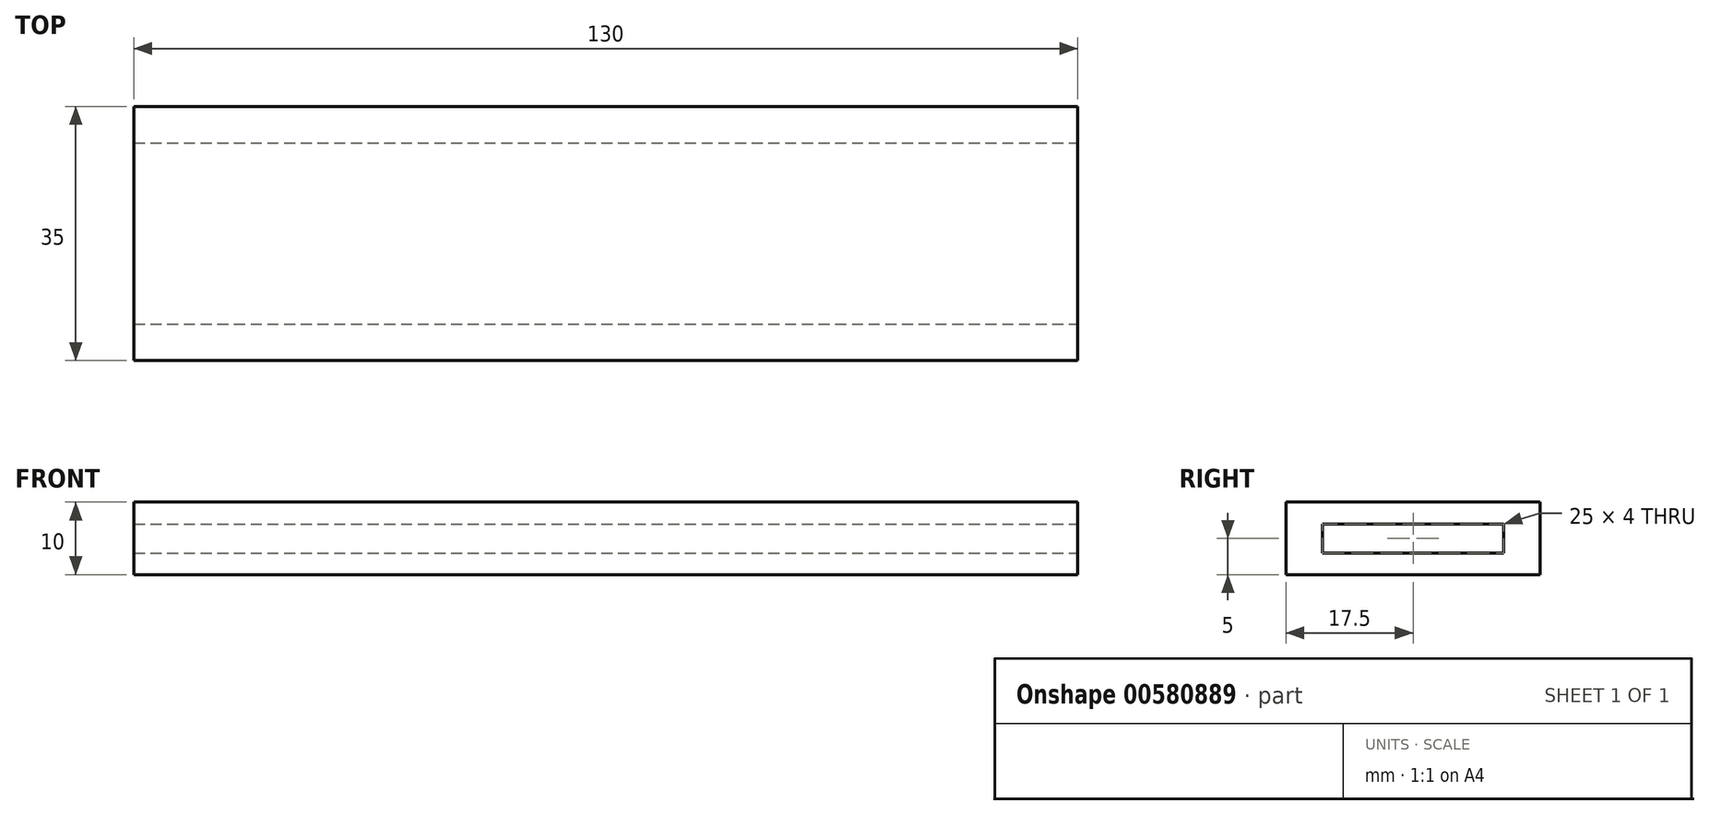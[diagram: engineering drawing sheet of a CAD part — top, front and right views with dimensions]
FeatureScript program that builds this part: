
annotation { "Feature Type Name" : "Feature", "Feature Type Description" : "" }
export const myFeature = defineFeature(function(context is Context, id is Id, definition is map)
    precondition{}
    {
        {
            var Q0;
            Q0=qCreatedBy(makeId("Top.planeOp"),FACE);
            var sketch = newSketch(context, id + "F0", { "sketchPlane" : qUnion([Q0])});
            skLineSegment(sketch, "E0.bottom", {"start": v(65, 17.5) * mm, "end": v(-65, 17.5) * mm});
            skLineSegment(sketch, "E0.top", {"start": v(65, -17.5) * mm, "end": v(-65, -17.5) * mm});
            skLineSegment(sketch, "E0.left", {"start": v(65, 17.5) * mm, "end": v(65, -17.5) * mm});
            skLineSegment(sketch, "E0.right", {"start": v(-65, 17.5) * mm, "end": v(-65, -17.5) * mm});
            skPoint(sketch, "E0.middle", {"position": v(0, 0) * mm});
            skLineSegment(sketch, "E1", {"start": v(-65, 12.5) * mm, "end": v(65, 12.5) * mm});
            skLineSegment(sketch, "E2", {"start": v(-65, -12.5) * mm, "end": v(65, -12.5) * mm});
            skSolve(sketch);
        }
        {
            var Q0;
            {var subQ0=sQuery(id+"F0.wireOp",EDGE,"E0.bottom");Q0=makeQuery(id+"F0.imprint","IMPRINT",FACE,{"disambiguationData":[TD([[makeQuery(id+"F0.imprint","IMPRINT",EDGE,{"derivedFrom":subQ0}),1.0]])]});}
            var Q1;
            {var subQ0=sQuery(id+"F0.wireOp",EDGE,"E1");Q1=makeQuery(id+"F0.imprint","IMPRINT",FACE,{"disambiguationData":[TD([[makeQuery(id+"F0.imprint","IMPRINT",EDGE,{"derivedFrom":subQ0}),-1.0]])]});}
            var Q2;
            {var subQ0=sQuery(id+"F0.wireOp",EDGE,"E0.top");Q2=makeQuery(id+"F0.imprint","IMPRINT",FACE,{"disambiguationData":[TD([[makeQuery(id+"F0.imprint","IMPRINT",EDGE,{"derivedFrom":subQ0}),-1.0]])]});}
            extrude(context, id + "F1", {"entities" : qUnion([Q0, Q1, Q2]), "depth" : 3 * mm, "offsetDistance" : 25 * mm});
        }
        {
            var Q0;
            Q0=makeQuery(id+"F1.opExtrude","CAP_FACE",FACE,{"disambiguationData":[OSD([sQuery(id+"F0.wireOp",EDGE,"E0.bottom"),sQuery(id+"F0.wireOp",EDGE,"E0.top"),sQuery(id+"F0.wireOp",EDGE,"E0.left"),sQuery(id+"F0.wireOp",EDGE,"E0.right")])],"isStart":false});
            var sketch = newSketch(context, id + "F2", { "sketchPlane" : qUnion([Q0])});
            skLineSegment(sketch, "E3.0.0", {"start": v(-65, 17.5) * mm, "end": v(-65, -17.5) * mm});
            skLineSegment(sketch, "E3.0.1", {"start": v(-65, -17.5) * mm, "end": v(65, -17.5) * mm});
            skLineSegment(sketch, "E3.0.2", {"start": v(65, -17.5) * mm, "end": v(65, 17.5) * mm});
            skLineSegment(sketch, "E3.0.3", {"start": v(65, 17.5) * mm, "end": v(-65, 17.5) * mm});
            skLineSegment(sketch, "E4.0", {"start": v(-65, 12.5) * mm, "end": v(65, 12.5) * mm});
            skLineSegment(sketch, "E4.1", {"start": v(-65, -12.5) * mm, "end": v(65, -12.5) * mm});
            skSolve(sketch);
        }
        {
            var Q0;
            {var subQ0=sQuery(id+"F2.wireOp",EDGE,"E3.0.3");Q0=makeQuery(id+"F2.imprint","IMPRINT",FACE,{"disambiguationData":[TD([[makeQuery(id+"F2.imprint","IMPRINT",EDGE,{"derivedFrom":subQ0}),1.0]])]});}
            extrude(context, id + "F3", {"entities" : qUnion([Q0]), "operationType" : NewBodyOperationType.ADD, "depth" : 7 * mm, "offsetDistance" : 25 * mm});
        }
        {
            var Q0;
            Q0=makeQuery(id+"F1.opExtrude","CAP_FACE",FACE,{"disambiguationData":[OSD([sQuery(id+"F0.wireOp",EDGE,"E0.bottom"),sQuery(id+"F0.wireOp",EDGE,"E0.top"),sQuery(id+"F0.wireOp",EDGE,"E0.left"),sQuery(id+"F0.wireOp",EDGE,"E0.right")])],"isStart":false});
            var sketch = newSketch(context, id + "F4", { "sketchPlane" : qUnion([Q0])});
            skLineSegment(sketch, "E5.0", {"start": v(-65, 12.5) * mm, "end": v(65, 12.5) * mm});
            skLineSegment(sketch, "E6.0.0", {"start": v(65, 12.5) * mm, "end": v(-65, 12.5) * mm});
            skLineSegment(sketch, "E6.0.1", {"start": v(-65, 12.5) * mm, "end": v(-65, -17.5) * mm});
            skLineSegment(sketch, "E6.0.2", {"start": v(-65, -17.5) * mm, "end": v(65, -17.5) * mm});
            skLineSegment(sketch, "E6.0.3", {"start": v(65, -17.5) * mm, "end": v(65, 12.5) * mm});
            skLineSegment(sketch, "E7.0", {"start": v(-65, -12.5) * mm, "end": v(65, -12.5) * mm});
            skSolve(sketch);
        }
        {
            var Q0;
            {var subQ0=sQuery(id+"F4.wireOp",EDGE,"E6.0.2");Q0=makeQuery(id+"F4.imprint","IMPRINT",FACE,{"disambiguationData":[TD([[makeQuery(id+"F4.imprint","IMPRINT",EDGE,{"derivedFrom":subQ0}),-1.0]])]});}
            extrude(context, id + "F5", {"entities" : qUnion([Q0]), "operationType" : NewBodyOperationType.ADD, "depth" : 4 * mm, "offsetDistance" : 25 * mm});
        }
        {
            var Q0;
            Q0=makeQuery(id+"F3.opExtrude","SWEPT_FACE",FACE,{"disambiguationData":[OSD([sQuery(id+"F2.wireOp",EDGE,"E4.0")])]});
            var sketch = newSketch(context, id + "F6", { "sketchPlane" : qUnion([Q0])});
            skLineSegment(sketch, "E8.0", {"start": v(-65, 10) * mm, "end": v(65, 10) * mm});
            skLineSegment(sketch, "E9.0.0", {"start": v(-65, 3) * mm, "end": v(65, 3) * mm});
            skLineSegment(sketch, "E9.0.1", {"start": v(65, 3) * mm, "end": v(65, 10) * mm});
            skLineSegment(sketch, "E9.0.2", {"start": v(65, 10) * mm, "end": v(-65, 10) * mm});
            skLineSegment(sketch, "E9.0.3", {"start": v(-65, 10) * mm, "end": v(-65, 3) * mm});
            skLineSegment(sketch, "E10.top", {"start": v(-65, 7) * mm, "end": v(65, 7) * mm});
            skLineSegment(sketch, "E10.left", {"start": v(-65, 10) * mm, "end": v(-65, 7) * mm});
            skLineSegment(sketch, "E10.right", {"start": v(65, 10) * mm, "end": v(65, 7) * mm});
            skSolve(sketch);
        }
        {
            var Q0;
            Q0=makeQuery(id+"F6.imprint","IMPRINT",FACE,{"disambiguationData":[TD([[makeQuery(id+"F6.imprint","IMPRINT",EDGE,{"derivedFrom":sQuery(id+"F6.wireOp",EDGE,"E8.0")}),-1.0]])]});
            extrude(context, id + "F7", {"entities" : qUnion([Q0]), "operationType" : NewBodyOperationType.ADD, "depth" : 30 * mm, "offsetDistance" : 25 * mm});
        }
    });
